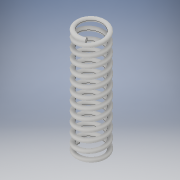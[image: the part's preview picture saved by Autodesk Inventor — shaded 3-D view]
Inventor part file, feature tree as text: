
AUTODESK INVENTOR PART (.ipt)
format: ipt  version: 2018 (Build 220112000, 112)  size: 465,408 bytes
history: native  units: in
note: dims shown in document units (in); Inventor stores cm internally (conversion verified against a paired STEP export)
features: helix x1, sketch x1
ambient origin geometry x8: Origin, YZ Plane, XZ Plane, XY Plane, X Axis, Y Axis, Z Axis, Center Point
bodies: Solid1 (feature_tree)
feature tree (2):
  helix  "Coil1"  [1 undecoded]
  sketch  "Sketch1"  dims[d1=0.077in d2=1.0in d3=0.517in d4=4.3307in d5=0.0in d6=90.0deg d7=150.0deg d8=90.0deg d9=150.0deg]
note: 1 required parameter value undecoded (feature->parameter linkage not recoverable at this tier; creation-order binding heuristic only, values carry confidence <= 0.55)
